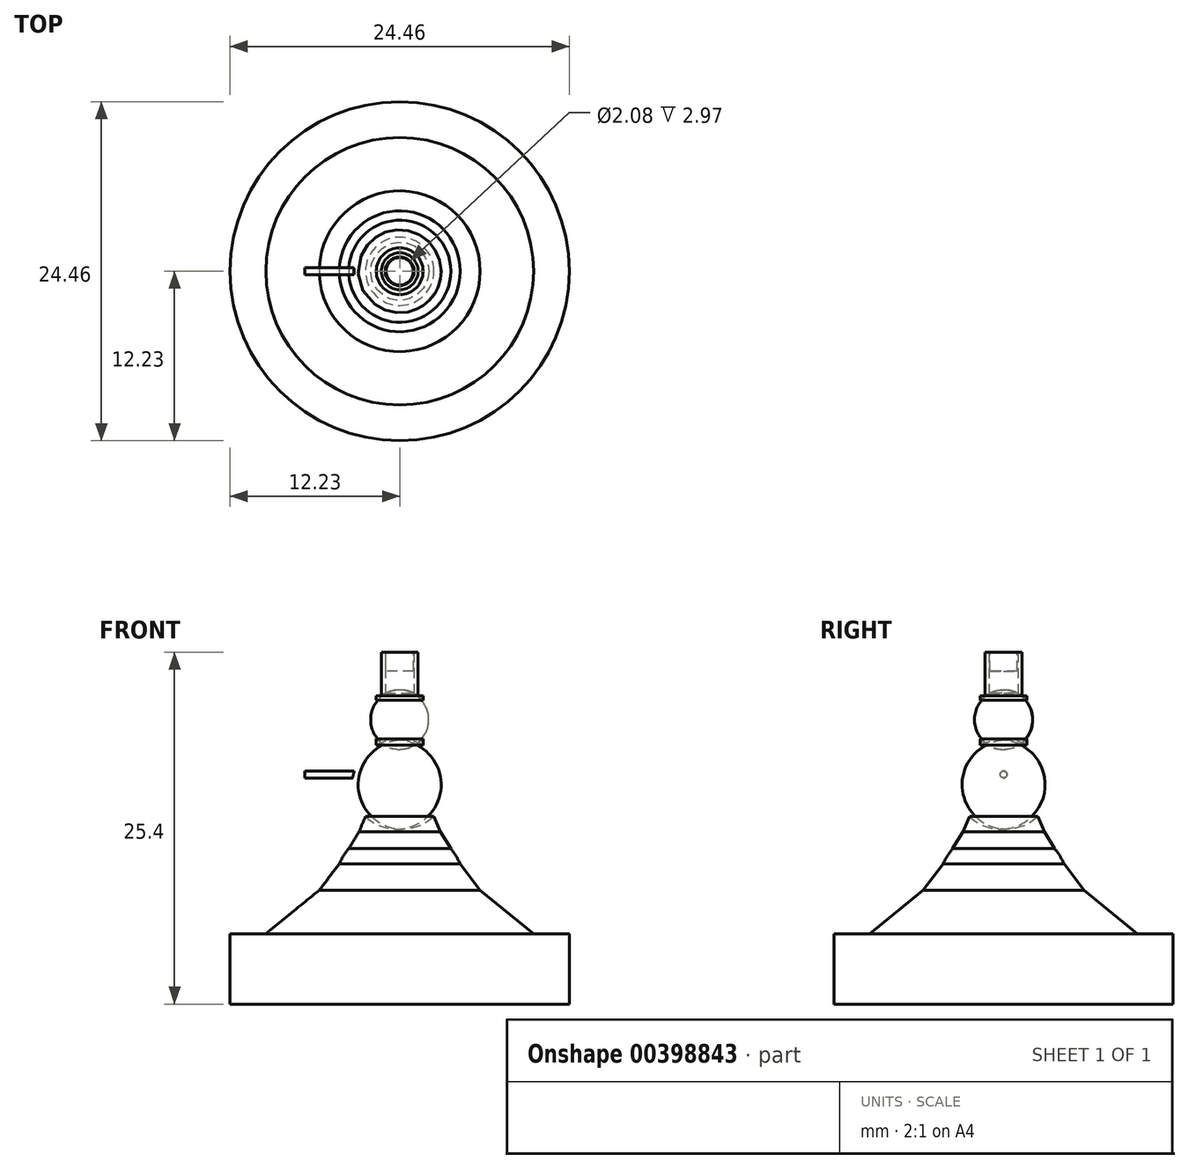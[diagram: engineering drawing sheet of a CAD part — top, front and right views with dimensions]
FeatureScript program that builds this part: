
annotation { "Feature Type Name" : "Feature", "Feature Type Description" : "" }
export const myFeature = defineFeature(function(context is Context, id is Id, definition is map)
    precondition{}
    {
        {
            var Q0;
            Q0=qCreatedBy(makeId("Top.planeOp"),FACE);
            var sketch = newSketch(context, id + "F0", { "sketchPlane" : qUnion([Q0])});
            skCircle(sketch, "E0", {"center": v(0, 0) * mm, "radius": 12.23 * mm});
            skSolve(sketch);
        }
        {
            var Q0;
            Q0 = qSketchRegion(id + "F0", true);
            extrude(context, id + "F1", {"entities" : qUnion([Q0]), "depth" : 5.08 * mm});
        }
        {
            var Q0;
            Q0=qCreatedBy(makeId("Front.planeOp"),FACE);
            var sketch = newSketch(context, id + "F2", { "sketchPlane" : qUnion([Q0])});
            skLineSegment(sketch, "E1", {"start": v(0, 0) * mm, "end": v(0, 12.95) * mm});
            skArc(sketch, "E2", {"start": v(0, 12.95) * mm, "mid": v(-1.78, 3.75) * mm, "end": v(3.3, 11.63) * mm});
            skSolve(sketch);
        }
        {
            var Q0;
            {var subQ0=sQuery(id+"F2.wireOp",EDGE,"E2");var subQ1=sQuery(id+"F2.wireOp",EDGE,"E1");var subQ2=makeQuery(id+"F2.imprint","INTERSECT",VERTEX,{"disambiguationData":[OD(0.0)],"derivedFrom":[subQ1,subQ0]});Q0=makeQuery(id+"F2.imprint","IMPRINT",FACE,{"disambiguationData":[TD([[makeQuery(id+"F2.imprint","IMPRINT",EDGE,{"disambiguationData":[TD([[subQ2,1.0]])],"derivedFrom":subQ1}),1.0]])]});}
            var Q1;
            Q1=sQuery(id+"F2.wireOp",EDGE,"E1");
            revolve(context, id + "F3", {"operationType" : NewBodyOperationType.ADD, "entities" : qUnion([Q0]), "axis" : qUnion([Q1]), "revolveType" : RevolveType.FULL});
        }
        {
            var Q0;
            Q0=qCreatedBy(makeId("Front.planeOp"),FACE);
            var sketch = newSketch(context, id + "F4", { "sketchPlane" : qUnion([Q0])});
            skLineSegment(sketch, "E3", {"start": v(0, 0) * mm, "end": v(0, 19.04) * mm});
            skArc(sketch, "E4", {"start": v(-2.7, 14.5) * mm, "mid": v(2.98, 14.2) * mm, "end": v(0, 19.04) * mm});
            skSolve(sketch);
        }
        {
            var Q0;
            {var subQ0=sQuery(id+"F4.wireOp",EDGE,"E4");var subQ1=sQuery(id+"F4.wireOp",EDGE,"E3");var subQ2=makeQuery(id+"F4.imprint","INTERSECT",VERTEX,{"disambiguationData":[OD(0.0)],"derivedFrom":[subQ1,subQ0]});Q0=makeQuery(id+"F4.imprint","IMPRINT",FACE,{"disambiguationData":[TD([[makeQuery(id+"F4.imprint","IMPRINT",EDGE,{"disambiguationData":[TD([[subQ2,1.0]])],"derivedFrom":subQ1}),-1.0]])]});}
            var Q1;
            Q1=sQuery(id+"F4.wireOp",EDGE,"E3");
            revolve(context, id + "F5", {"operationType" : NewBodyOperationType.ADD, "entities" : qUnion([Q0]), "axis" : qUnion([Q1]), "revolveType" : RevolveType.FULL});
        }
        {
            var Q0;
            Q0=qCreatedBy(makeId("Front.planeOp"),FACE);
            var sketch = newSketch(context, id + "F6", { "sketchPlane" : qUnion([Q0])});
            skLineSegment(sketch, "E5", {"start": v(0, 0) * mm, "end": v(0, 23.86) * mm});
            skArc(sketch, "E6", {"start": v(0, 22.67) * mm, "mid": v(-0.86, 18.53) * mm, "end": v(1.41, 22.1) * mm});
            skSolve(sketch);
        }
        {
            var Q0;
            {var subQ0=sQuery(id+"F6.wireOp",EDGE,"E6");var subQ1=sQuery(id+"F6.wireOp",EDGE,"E5");var subQ2=makeQuery(id+"F6.imprint","INTERSECT",VERTEX,{"disambiguationData":[OD(0.0)],"derivedFrom":[subQ1,subQ0]});Q0=makeQuery(id+"F6.imprint","IMPRINT",FACE,{"disambiguationData":[TD([[makeQuery(id+"F6.imprint","IMPRINT",EDGE,{"disambiguationData":[TD([[subQ2,1.0]])],"derivedFrom":subQ1}),1.0]])]});}
            var Q1;
            Q1=sQuery(id+"F6.wireOp",EDGE,"E5");
            revolve(context, id + "F7", {"operationType" : NewBodyOperationType.ADD, "entities" : qUnion([Q0]), "axis" : qUnion([Q1]), "revolveType" : RevolveType.FULL});
        }
        {
            var Q0;
            Q0=qCreatedBy(makeId("Right.planeOp"),FACE);
            var sketch = newSketch(context, id + "F8", { "sketchPlane" : qUnion([Q0])});
            skCircle(sketch, "E7", {"center": v(0, 16.57) * mm, "radius": 0.25 * mm});
            skSolve(sketch);
        }
        {
            var Q0;
            Q0=makeQuery(id+"F8.imprint","IMPRINT",FACE,{"disambiguationData":[TD([[makeQuery(id+"F8.imprint","IMPRINT",EDGE,{"derivedFrom":sQuery(id+"F8.wireOp",EDGE,"E7")}),1.0]])]});
            extrude(context, id + "F9", {"entities" : qUnion([Q0]), "operationType" : NewBodyOperationType.ADD, "depth" : 7.06 * mm});
        }
        {
            var Q0;
            Q0=makeQuery(id+"F9.opExtrude","CAP_FACE",FACE,{"disambiguationData":[OSD([sQuery(id+"F8.wireOp",EDGE,"E7")])],"isStart":false});
            extrude(context, id + "F10", {"entities" : qUnion([Q0]), "operationType" : NewBodyOperationType.ADD, "oppositeDirection" : true, "depth" : 13.92 * mm});
        }
        {
            var Q0;
            Q0=makeQuery(id+"F1.opExtrude","CAP_FACE",FACE,{"disambiguationData":[OSD([sQuery(id+"F0.wireOp",EDGE,"E0")])],"isStart":false});
            var sketch = newSketch(context, id + "F11", { "sketchPlane" : qUnion([Q0])});
            skCircle(sketch, "E8", {"center": v(0, 0) * mm, "radius": 1.69 * mm});
            skSolve(sketch);
        }
        {
            var Q0;
            Q0=makeQuery(id+"F11.imprint","IMPRINT",FACE,{"disambiguationData":[TD([[makeQuery(id+"F11.imprint","IMPRINT",EDGE,{"derivedFrom":sQuery(id+"F11.wireOp",EDGE,"E8")}),1.0]])]});
            extrude(context, id + "F12", {"entities" : qUnion([Q0]), "operationType" : NewBodyOperationType.ADD, "depth" : 17.17 * mm});
        }
        {
            var Q0;
            Q0=makeQuery(id+"F12.opExtrude","CAP_FACE",FACE,{"disambiguationData":[OSD([sQuery(id+"F11.wireOp",EDGE,"E8")])],"isStart":false});
            var sketch = newSketch(context, id + "F13", { "sketchPlane" : qUnion([Q0])});
            skCircle(sketch, "E9", {"center": v(0, 0) * mm, "radius": 1.04 * mm});
            skSolve(sketch);
        }
        {
            var Q0;
            Q0=makeQuery(id+"F13.imprint","IMPRINT",FACE,{"disambiguationData":[TD([[makeQuery(id+"F13.imprint","IMPRINT",EDGE,{"derivedFrom":sQuery(id+"F13.wireOp",EDGE,"E9")}),-1.0]])]});
            extrude(context, id + "F14", {"entities" : qUnion([Q0]), "operationType" : NewBodyOperationType.ADD, "depth" : 3.15 * mm});
        }
        {
            var Q0;
            Q0=makeQuery(id+"F3.opRevolve","SWEPT_FACE",FACE,{"disambiguationData":[OSD([sQuery(id+"F2.wireOp",EDGE,"E2")])]});
            chamfer(context, id + "F15", {"entities" : qUnion([Q0]), "width" : 5.08 * mm, "tangentPropagation" : true});
        }
        {
            var Q0;
            Q0=makeQuery(id+"F3.opRevolve","SWEPT_FACE",FACE,{"disambiguationData":[OSD([sQuery(id+"F2.wireOp",EDGE,"E2")])]});
            chamfer(context, id + "F16", {"entities" : qUnion([Q0]), "width" : 5.08 * mm, "tangentPropagation" : true});
        }
        {
            var Q0;
            Q0=makeQuery(id+"F14.opExtrude","CAP_FACE",FACE,{"disambiguationData":[OSD([sQuery(id+"F6.wireOp",EDGE,"E6"),sQuery(id+"F11.wireOp",EDGE,"E8"),sQuery(id+"F13.wireOp",EDGE,"E9")])],"isStart":false});
            var sketch = newSketch(context, id + "F17", { "sketchPlane" : qUnion([Q0])});
            skCircle(sketch, "E10", {"center": v(0, 0) * mm, "radius": 0.99 * mm});
            skSolve(sketch);
        }
        {
            var Q0;
            Q0=makeQuery(id+"F17.imprint","IMPRINT",FACE,{"disambiguationData":[TD([[makeQuery(id+"F17.imprint","IMPRINT",EDGE,{"derivedFrom":sQuery(id+"F17.wireOp",EDGE,"E10")}),1.0]])]});
            extrude(context, id + "F18", {"entities" : qUnion([Q0]), "oppositeDirection" : true, "depth" : 1.37 * mm});
        }
    });
